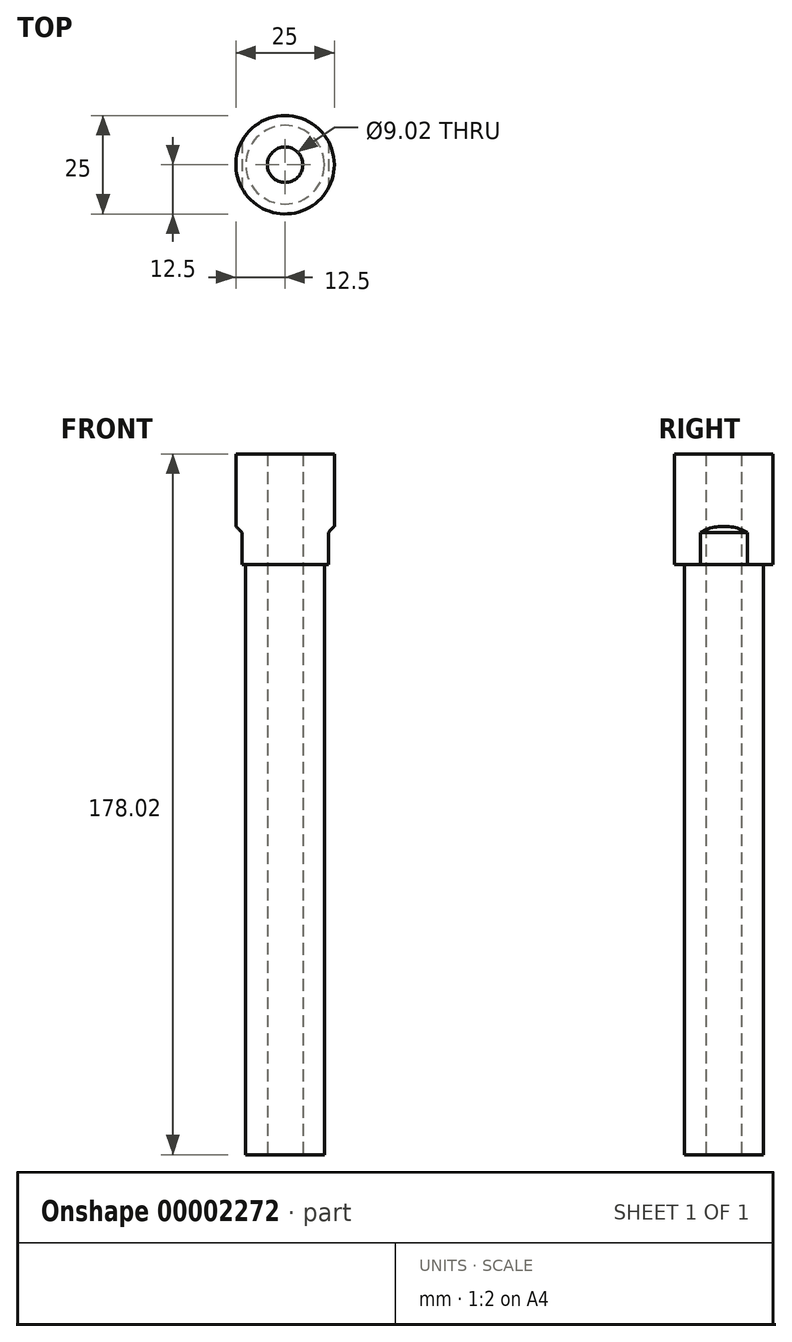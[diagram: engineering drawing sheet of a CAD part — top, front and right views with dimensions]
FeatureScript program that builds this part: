
annotation { "Feature Type Name" : "Feature", "Feature Type Description" : "" }
export const myFeature = defineFeature(function(context is Context, id is Id, definition is map)
    precondition{}
    {
        {
            var Q0;
            Q0=qCreatedBy(makeId("Top.planeOp"),FACE);
            var sketch = newSketch(context, id + "F0", { "sketchPlane" : qUnion([Q0])});
            skCircle(sketch, "E0", {"center": v(0, 0) * mm, "radius": 12.5 * mm});
            skCircle(sketch, "E1", {"center": v(0, 0) * mm, "radius": 10 * mm});
            skCircle(sketch, "E2", {"center": v(0, 0) * mm, "radius": 4.5 * mm});
            skSolve(sketch);
        }
        {
            var Q0;
            Q0=makeQuery(id+"F0.imprint","IMPRINT",FACE,{"disambiguationData":[TD([[makeQuery(id+"F0.imprint","IMPRINT",EDGE,{"derivedFrom":sQuery(id+"F0.wireOp",EDGE,"E0")}),1.0]])]});
            var Q1;
            Q1=makeQuery(id+"F0.imprint","IMPRINT",FACE,{"disambiguationData":[TD([[makeQuery(id+"F0.imprint","IMPRINT",EDGE,{"derivedFrom":sQuery(id+"F0.wireOp",EDGE,"E1")}),1.0]])]});
            extrude(context, id + "F1", {"entities" : qUnion([Q0, Q1]), "depth" : 28.02 * mm});
        }
        {
            var Q0;
            Q0=makeQuery(id+"F0.imprint","IMPRINT",FACE,{"disambiguationData":[TD([[makeQuery(id+"F0.imprint","IMPRINT",EDGE,{"derivedFrom":sQuery(id+"F0.wireOp",EDGE,"E1")}),1.0]])]});
            extrude(context, id + "F2", {"entities" : qUnion([Q0]), "operationType" : NewBodyOperationType.ADD, "oppositeDirection" : true, "depth" : 150 * mm});
        }
        {
            var Q0;
            Q0=qCreatedBy(makeId("Front.planeOp"),FACE);
            var sketch = newSketch(context, id + "F3", { "sketchPlane" : qUnion([Q0])});
            skLineSegment(sketch, "E3.bottom", {"start": v(10.99, 0) * mm, "end": v(21.89, 0) * mm});
            skLineSegment(sketch, "E3.top", {"start": v(10.99, 9.65) * mm, "end": v(21.89, 9.65) * mm});
            skLineSegment(sketch, "E3.left", {"start": v(10.99, 0) * mm, "end": v(10.99, 9.65) * mm});
            skLineSegment(sketch, "E3.right", {"start": v(21.89, 0) * mm, "end": v(21.89, 9.65) * mm});
            skLineSegment(sketch, "E4", {"start": v(0, 0) * mm, "end": v(0, 8.23) * mm, "construction": true});
            skLineSegment(sketch, "E5.0.MirrorCS", {"start": v(-10.99, 0) * mm, "end": v(-10.99, 9.65) * mm});
            skLineSegment(sketch, "E6.0.MirrorCS", {"start": v(-10.99, 0) * mm, "end": v(-21.89, 0) * mm});
            skLineSegment(sketch, "E7.0.MirrorCS", {"start": v(-10.99, 9.65) * mm, "end": v(-21.89, 9.65) * mm});
            skLineSegment(sketch, "E8.0.MirrorCS", {"start": v(-21.89, 0) * mm, "end": v(-21.89, 9.65) * mm});
            skSolve(sketch);
        }
        {
            var Q0;
            Q0 = qSketchRegion(id + "F3", true);
            extrude(context, id + "F4", {"entities" : qUnion([Q0]), "operationType" : NewBodyOperationType.REMOVE, "endBound" : BoundingType.SYMMETRIC, "oppositeDirection" : true, "depth" : 25.4 * mm});
        }
        {
            var Q0;
            Q0=makeQuery(id+"F4.boolean.opBoolean","COPY",EDGE,{"derivedFrom":makeQuery(id+"F4.opExtrude","SWEPT_EDGE",EDGE,{"disambiguationData":[OSD([sQuery(id+"F3.wireOp",EDGE,"E3.top"),sQuery(id+"F3.wireOp",EDGE,"E3.left")])]})});
            var Q1;
            Q1=makeQuery(id+"F4.boolean.opBoolean","COPY",EDGE,{"derivedFrom":makeQuery(id+"F4.opExtrude","SWEPT_EDGE",EDGE,{"disambiguationData":[OSD([sQuery(id+"F3.wireOp",EDGE,"E5.0.MirrorCS"),sQuery(id+"F3.wireOp",EDGE,"E7.0.MirrorCS")])]})});
            chamfer(context, id + "F5", {"entities" : qUnion([Q0, Q1]), "width" : 1.52 * mm});
        }
    });
